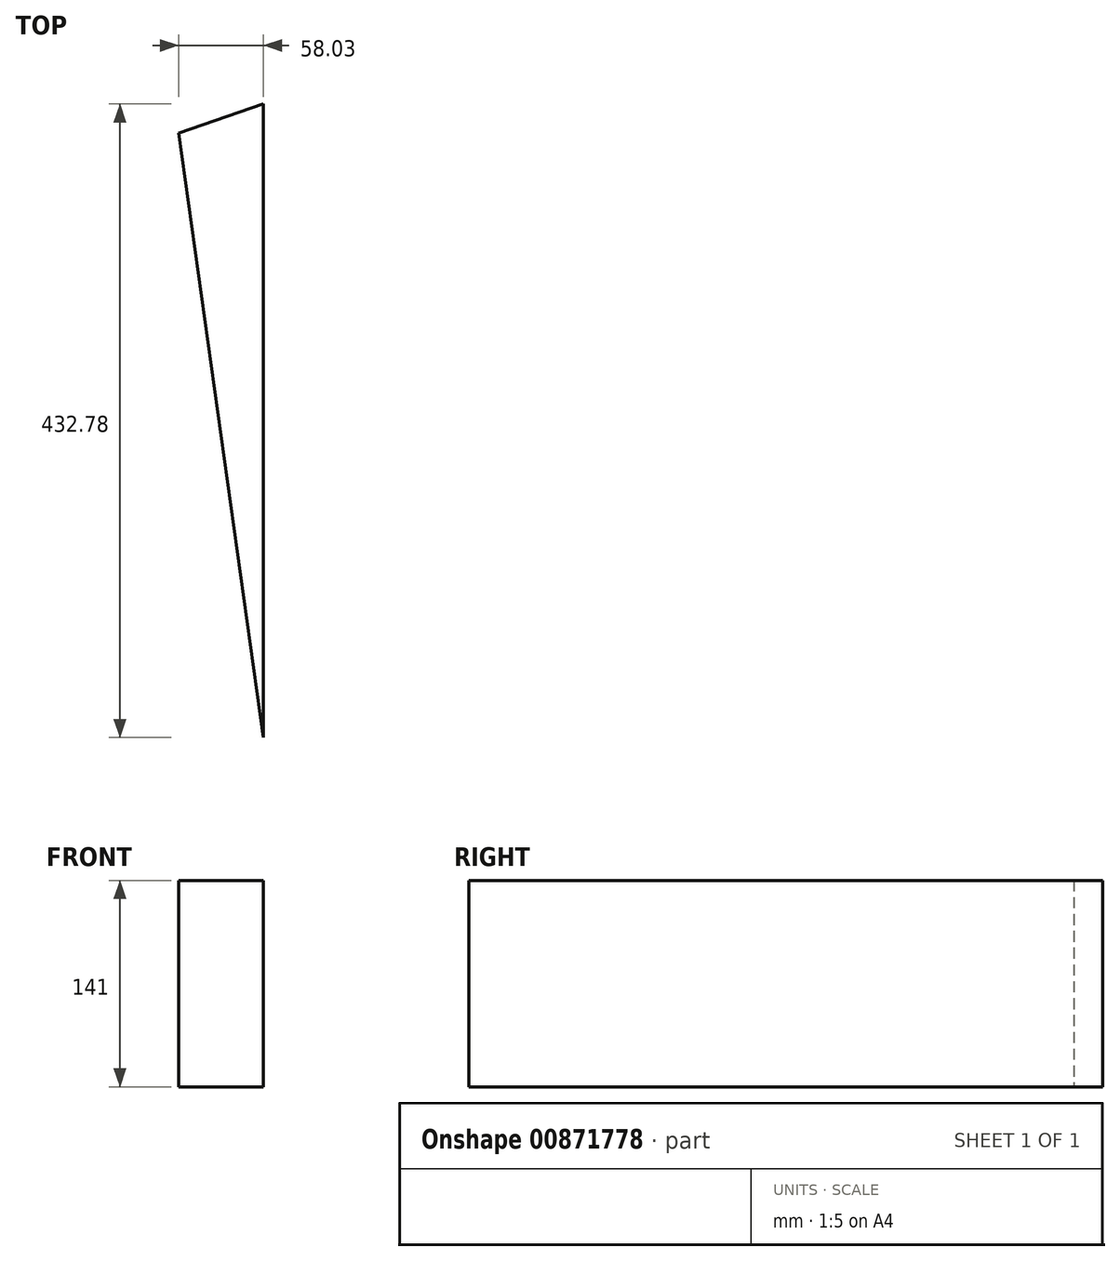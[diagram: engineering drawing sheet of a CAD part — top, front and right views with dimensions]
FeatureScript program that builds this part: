
annotation { "Feature Type Name" : "Feature", "Feature Type Description" : "" }
export const myFeature = defineFeature(function(context is Context, id is Id, definition is map)
    precondition{}
    {
        {
            var Q0;
            Q0=qCreatedBy(makeId("Top.planeOp"),FACE);
            var sketch = newSketch(context, id + "F0", { "sketchPlane" : qUnion([Q0])});
            skLineSegment(sketch, "E0", {"start": v(0, 0) * mm, "end": v(0, 48.8) * mm});
            skLineSegment(sketch, "E1", {"start": v(0, 0) * mm, "end": v(-9.22, 65.6) * mm});
            skLineSegment(sketch, "E2", {"start": v(-9.22, 65.6) * mm, "end": v(0, 65.6) * mm});
            skLineSegment(sketch, "E3", {"start": v(0, 65.6) * mm, "end": v(0, 48.8) * mm});
            skLineSegment(sketch, "E4", {"start": v(-9.22, 65.6) * mm, "end": v(-58.03, 412.9) * mm});
            skLineSegment(sketch, "E5", {"start": v(-58.03, 412.9) * mm, "end": v(273.41, 526.42) * mm});
            skLineSegment(sketch, "E6", {"start": v(0, 65.6) * mm, "end": v(0, 475.74) * mm});
            skSolve(sketch);
        }
        {
            var Q0;
            Q0 = qSketchRegion(id + "F0", true);
            extrude(context, id + "F1", {"entities" : qUnion([Q0]), "depth" : 141 * mm, "offsetDistance" : 25 * mm});
        }
    });
